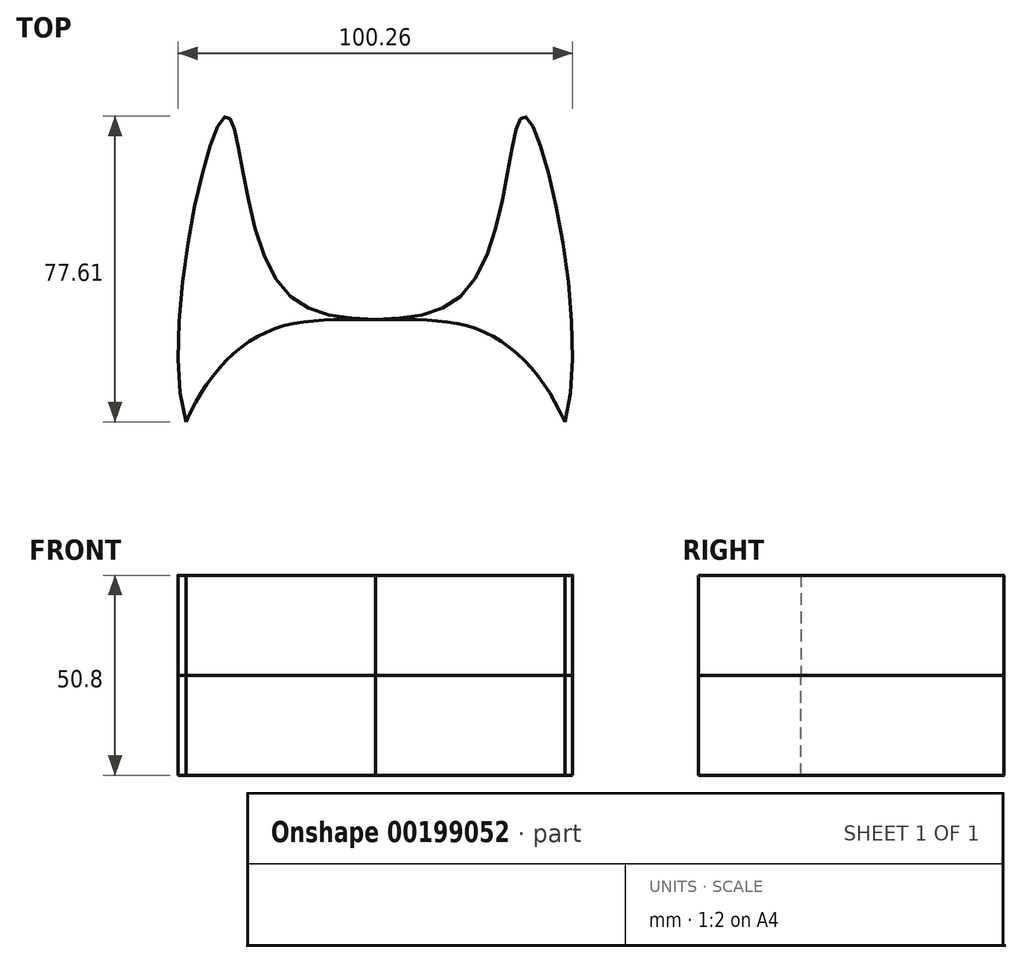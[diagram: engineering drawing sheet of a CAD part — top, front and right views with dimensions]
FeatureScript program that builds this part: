
annotation { "Feature Type Name" : "Feature", "Feature Type Description" : "" }
export const myFeature = defineFeature(function(context is Context, id is Id, definition is map)
    precondition{}
    {
        {
            var Q0;
            Q0=qCreatedBy(makeId("Top.planeOp"),FACE);
            var sketch = newSketch(context, id + "F0", { "sketchPlane" : qUnion([Q0])});
            skFitSpline(sketch, "E0", {"points": [v(-54.17, -31.88) * mm, v(-25.4, 15.64) * mm, v(23.8, 26.1) * mm, v(38.1, 69.47) * mm, v(45.24, -13.96) * mm, v(-11.11, -11.43) * mm, v(-48, -55.98) * mm, v(-54.17, -31.88) * mm]});
            skFitSpline(sketch, "E1.MirrorC", {"points": [v(54.17, -31.88) * mm, v(25.4, 15.64) * mm, v(-23.8, 26.1) * mm, v(-38.1, 69.47) * mm, v(-45.24, -13.96) * mm, v(11.11, -11.43) * mm, v(48, -55.98) * mm, v(54.17, -31.88) * mm]});
            skSolve(sketch);
        }
        {
            var Q0;
            {var subQ0=sQuery(id+"F0.wireOp",EDGE,"E1.MirrorC");var subQ1=sQuery(id+"F0.wireOp",EDGE,"E0");var subQ2=makeQuery(id+"F0.imprint","INTERSECT",VERTEX,{"disambiguationData":[OD(0.0)],"derivedFrom":[subQ1,subQ0]});Q0=makeQuery(id+"F0.imprint","IMPRINT",FACE,{"disambiguationData":[TD([[makeQuery(id+"F0.imprint","IMPRINT",EDGE,{"disambiguationData":[TD([[subQ2,1.0]])],"derivedFrom":subQ1}),1.0]])]});}
            var Q1;
            {var subQ0=sQuery(id+"F0.wireOp",EDGE,"E1.MirrorC");var subQ1=sQuery(id+"F0.wireOp",EDGE,"E0");var subQ2=makeQuery(id+"F0.imprint","INTERSECT",VERTEX,{"disambiguationData":[OD(0.0)],"derivedFrom":[subQ1,subQ0]});Q1=makeQuery(id+"F0.imprint","IMPRINT",FACE,{"disambiguationData":[TD([[makeQuery(id+"F0.imprint","IMPRINT",EDGE,{"disambiguationData":[TD([[subQ2,-1.0]])],"derivedFrom":subQ1}),-1.0]])]});}
            extrude(context, id + "F1", {"entities" : qUnion([Q0, Q1]), "depth" : 25.4 * mm});
        }
        {
            var Q0;
            {var subQ0=sQuery(id+"F0.wireOp",EDGE,"E1.MirrorC");var subQ1=sQuery(id+"F0.wireOp",EDGE,"E0");var subQ2=makeQuery(id+"F0.imprint","INTERSECT",VERTEX,{"disambiguationData":[OD(0.0)],"derivedFrom":[subQ1,subQ0]});Q0=makeQuery(id+"F1.opExtrude","CAP_FACE",FACE,{"disambiguationData":[OSD([subQ1,subQ0]),TDD([makeQuery(id+"F0.imprint","IMPRINT",EDGE,{"disambiguationData":[TD([[subQ2,-1.0]])],"derivedFrom":subQ1}),makeQuery(id+"F0.imprint","IMPRINT",EDGE,{"disambiguationData":[TD([[subQ2,1.0]])],"derivedFrom":subQ0})])],"isStart":true});}
            var Q1;
            {var subQ0=sQuery(id+"F0.wireOp",EDGE,"E1.MirrorC");var subQ1=sQuery(id+"F0.wireOp",EDGE,"E0");var subQ2=makeQuery(id+"F0.imprint","INTERSECT",VERTEX,{"disambiguationData":[OD(0.0)],"derivedFrom":[subQ1,subQ0]});Q1=makeQuery(id+"F1.opExtrude","CAP_FACE",FACE,{"disambiguationData":[OSD([subQ1,subQ0]),TDD([makeQuery(id+"F0.imprint","IMPRINT",EDGE,{"disambiguationData":[TD([[subQ2,1.0]])],"derivedFrom":subQ1}),makeQuery(id+"F0.imprint","IMPRINT",EDGE,{"disambiguationData":[TD([[subQ2,-1.0]])],"derivedFrom":subQ0})])],"isStart":true});}
            extrude(context, id + "F2", {"entities" : qUnion([Q0, Q1]), "depth" : 25.4 * mm});
        }
    });
